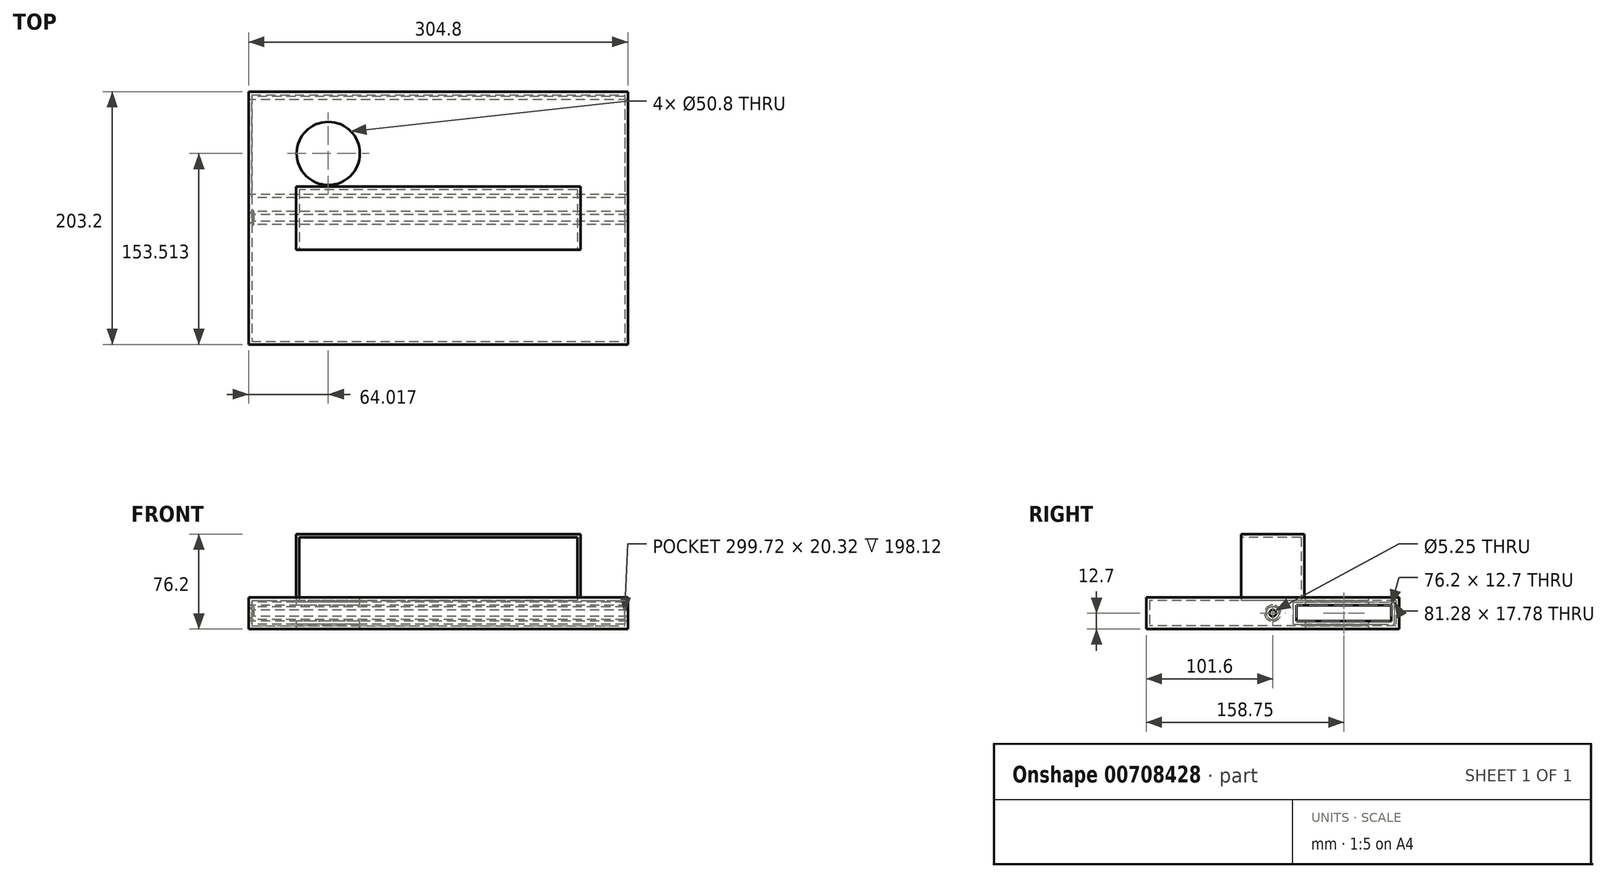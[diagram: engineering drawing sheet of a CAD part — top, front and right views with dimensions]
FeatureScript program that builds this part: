
annotation { "Feature Type Name" : "Feature", "Feature Type Description" : "" }
export const myFeature = defineFeature(function(context is Context, id is Id, definition is map)
    precondition{}
    {
        {
            var Q0;
            Q0=qCreatedBy(makeId("Top.planeOp"),FACE);
            var sketch = newSketch(context, id + "F0", { "sketchPlane" : qUnion([Q0])});
            skLineSegment(sketch, "E0.bottom", {"start": v(-152.4, 101.6) * mm, "end": v(152.4, 101.6) * mm});
            skLineSegment(sketch, "E0.top", {"start": v(-152.4, -101.6) * mm, "end": v(152.4, -101.6) * mm});
            skLineSegment(sketch, "E0.left", {"start": v(-152.4, 101.6) * mm, "end": v(-152.4, -101.6) * mm});
            skLineSegment(sketch, "E0.right", {"start": v(152.4, 101.6) * mm, "end": v(152.4, -101.6) * mm});
            skPoint(sketch, "E0.middle", {"position": v(0, 0) * mm});
            skSolve(sketch);
        }
        {
            var Q0;
            Q0=makeQuery(id+"F0.imprint","IMPRINT",FACE,{"disambiguationData":[TD([[makeQuery(id+"F0.imprint","IMPRINT",EDGE,{"derivedFrom":sQuery(id+"F0.wireOp",EDGE,"E0.bottom")}),-1.0]])]});
            extrude(context, id + "F1", {"entities" : qUnion([Q0]), "depth" : 25.4 * mm, "offsetDistance" : 25.4 * mm});
        }
        {
            var Q0;
            Q0=makeQuery(id+"F1.opExtrude","SWEPT_FACE",FACE,{"disambiguationData":[OSD([sQuery(id+"F0.wireOp",EDGE,"E0.left")])]});
            var sketch = newSketch(context, id + "F2", { "sketchPlane" : qUnion([Q0])});
            skLineSegment(sketch, "E1.bottom", {"start": v(-19.05, 6.35) * mm, "end": v(-95.25, 6.35) * mm});
            skLineSegment(sketch, "E1.top", {"start": v(-19.05, 19.05) * mm, "end": v(-95.25, 19.05) * mm});
            skLineSegment(sketch, "E1.left", {"start": v(-19.05, 6.35) * mm, "end": v(-19.05, 19.05) * mm});
            skLineSegment(sketch, "E1.right", {"start": v(-95.25, 6.35) * mm, "end": v(-95.25, 19.05) * mm});
            skPoint(sketch, "E1.middle", {"position": v(-57.15, 12.7) * mm});
            skPoint(sketch, "E1.middle.positionSnap0", {"position": v(-101.6, 12.7) * mm});
            skPoint(sketch, "E1.centerSnap0", {"position": v(-101.6, 12.7) * mm});
            skSolve(sketch);
        }
        {
            var Q0;
            Q0 = qSketchRegion(id + "F2", true);
            extrude(context, id + "F3", {"entities" : qUnion([Q0]), "operationType" : NewBodyOperationType.REMOVE, "oppositeDirection" : true, "depth" : 378.2 * mm, "offsetDistance" : 25.4 * mm});
        }
        {
            var Q0;
            Q0=makeQuery(id+"F1.opExtrude","CAP_FACE",FACE,{"disambiguationData":[OSD([sQuery(id+"F0.wireOp",EDGE,"E0.bottom"),sQuery(id+"F0.wireOp",EDGE,"E0.top"),sQuery(id+"F0.wireOp",EDGE,"E0.left"),sQuery(id+"F0.wireOp",EDGE,"E0.right")])],"isStart":false});
            var sketch = newSketch(context, id + "F4", { "sketchPlane" : qUnion([Q0])});
            skCircle(sketch, "E2", {"center": v(-88.38, 51.91) * mm, "radius": 25.4 * mm});
            skSolve(sketch);
        }
        {
            var Q0;
            Q0=makeQuery(id+"F1.opExtrude","SWEPT_FACE",FACE,{"disambiguationData":[OSD([sQuery(id+"F0.wireOp",EDGE,"E0.left")])]});
            var sketch = newSketch(context, id + "F5", { "sketchPlane" : qUnion([Q0])});
            skPoint(sketch, "E3", {"position": v(0, 12.7) * mm});
            skPoint(sketch, "E3.positionSnap0", {"position": v(-19.05, 12.7) * mm});
            skSolve(sketch);
        }
        {
            var Q0;
            Q0=sQuery(id+"F5.wireOp",VERTEX,"E3");
            var Q1;
            Q1=makeQuery(id+"F1.opExtrude","SWEPT_BODY",BODY,{"disambiguationData":[OSD([sQuery(id+"F0.wireOp",EDGE,"E0.bottom"),sQuery(id+"F0.wireOp",EDGE,"E0.top"),sQuery(id+"F0.wireOp",EDGE,"E0.left"),sQuery(id+"F0.wireOp",EDGE,"E0.right")])]});
            hole(context, id + "F6", {"style" : HoleStyle.C_SINK, "endStyle" : HoleEndStyle.THROUGH, "standardTappedOrClearance" : lookupTablePath({ "standard" : "ISO", "fit" : "Close", "size" : "M5", "type" : "Clearance" }), "standardBlindInLast" : lookupTablePath({ "fit" : "Close", "standard" : "ISO", "size" : "M5", "type" : "Clearance" }), "holeDiameter" : 5.25 * mm, "cSinkDiameter" : 11.2 * mm, "cSinkAngle" : 90 * degree, "majorDiameter" : 6.35 * mm, "isTappedThrough" : true, "tappedDepth" : 12.7 * mm, "tapClearance" : 3, "locations" : qUnion([Q0]), "scope" : qUnion([Q1])});
        }
        {
            var Q0;
            Q0=makeQuery(id+"F4.imprint","IMPRINT",FACE,{"disambiguationData":[TD([[makeQuery(id+"F4.imprint","IMPRINT",EDGE,{"derivedFrom":sQuery(id+"F4.wireOp",EDGE,"E2")}),-1.0]])]});
            var sketch = newSketch(context, id + "F7", { "sketchPlane" : qUnion([Q0])});
            skLineSegment(sketch, "E4.bottom", {"start": v(114.3, 25.4) * mm, "end": v(-114.3, 25.4) * mm});
            skLineSegment(sketch, "E4.top", {"start": v(114.3, -25.4) * mm, "end": v(-114.3, -25.4) * mm});
            skLineSegment(sketch, "E4.left", {"start": v(114.3, 25.4) * mm, "end": v(114.3, -25.4) * mm});
            skLineSegment(sketch, "E4.right", {"start": v(-114.3, 25.4) * mm, "end": v(-114.3, -25.4) * mm});
            skPoint(sketch, "E4.middle", {"position": v(0, 0) * mm});
            skSolve(sketch);
        }
        {
            var Q0;
            Q0=makeQuery(id+"F7.imprint","IMPRINT",FACE,{"disambiguationData":[TD([[makeQuery(id+"F7.imprint","IMPRINT",EDGE,{"derivedFrom":sQuery(id+"F7.wireOp",EDGE,"E4.bottom")}),1.0]])]});
            extrude(context, id + "F8", {"entities" : qUnion([Q0]), "operationType" : NewBodyOperationType.ADD, "depth" : 50.8 * mm, "offsetDistance" : 25.4 * mm});
        }
        {
            var Q0;
            Q0=makeQuery(id+"F8.opExtrude","SWEPT_FACE",FACE,{"disambiguationData":[OSD([sQuery(id+"F7.wireOp",EDGE,"E4.top")])]});
            var Q1;
            Q1=makeQuery(id+"F1.opExtrude","SWEPT_BODY",BODY,{"disambiguationData":[OSD([sQuery(id+"F0.wireOp",EDGE,"E0.bottom"),sQuery(id+"F0.wireOp",EDGE,"E0.top"),sQuery(id+"F0.wireOp",EDGE,"E0.left"),sQuery(id+"F0.wireOp",EDGE,"E0.right")])]});
            shell(context, id + "F9", {"entities" : qUnion([Q0]), "parts" : qUnion([Q1]), "thickness" : 2.54 * mm});
        }
        {
            var Q0;
            Q0=makeQuery(id+"F1.opExtrude","CAP_FACE",FACE,{"disambiguationData":[OSD([sQuery(id+"F0.wireOp",EDGE,"E0.bottom"),sQuery(id+"F0.wireOp",EDGE,"E0.top"),sQuery(id+"F0.wireOp",EDGE,"E0.left"),sQuery(id+"F0.wireOp",EDGE,"E0.right")])],"isStart":true});
            var sketch = newSketch(context, id + "F10", { "sketchPlane" : qUnion([Q0])});
            skLineSegment(sketch, "E5", {"start": v(0, 76.55) * mm, "end": v(0, -75.85) * mm});
            skSolve(sketch);
        }
        {
            var Q0;
            Q0=makeQuery(id+"F10.imprint","IMPRINT",FACE,{"disambiguationData":[TD([[makeQuery(id+"F10.imprint","IMPRINT",EDGE,{"derivedFrom":makeQuery(id+"F1.opExtrude","CAP_EDGE",EDGE,{"disambiguationData":[OSD([sQuery(id+"F0.wireOp",EDGE,"E0.bottom")])],"isStart":true})}),1.0]])]});
            var sketch = newSketch(context, id + "F11", { "sketchPlane" : qUnion([Q0])});
            skArc(sketch, "E6", {"start": v(0, 67.07) * mm, "mid": v(67.07, 0) * mm, "end": v(0, -67.07) * mm});
            skSolve(sketch);
        }
        {
            var Q0;
            Q0=makeQuery(id+"F10.imprint","IMPRINT",FACE,{"disambiguationData":[TD([[makeQuery(id+"F10.imprint","IMPRINT",EDGE,{"derivedFrom":makeQuery(id+"F1.opExtrude","CAP_EDGE",EDGE,{"disambiguationData":[OSD([sQuery(id+"F0.wireOp",EDGE,"E0.bottom")])],"isStart":true})}),1.0]])]});
            var Q1;
            Q1=sQuery(id+"F11.wireOp",EDGE,"E6");
            var Q2;
            Q2=sQuery(id+"F10.wireOp",EDGE,"E5");
            revolve(context, id + "F12", {"bodyType" : ToolBodyType.SURFACE, "operationType" : NewBodyOperationType.INTERSECT, "surfaceOperationType" : NewSurfaceOperationType.NEW, "entities" : qUnion([Q0]), "surfaceEntities" : qUnion([Q1]), "axis" : qUnion([Q2]), "revolveType" : RevolveType.ONE_DIRECTION, "angle" : 180 * degree});
        }
        {
            var Q0;
            Q0=makeQuery(id+"F4.imprint","IMPRINT",FACE,{"disambiguationData":[TD([[makeQuery(id+"F4.imprint","IMPRINT",EDGE,{"derivedFrom":sQuery(id+"F4.wireOp",EDGE,"E2")}),1.0]])]});
            extrude(context, id + "F13", {"entities" : qUnion([Q0]), "operationType" : NewBodyOperationType.REMOVE, "oppositeDirection" : true, "depth" : 25.4 * mm, "offsetDistance" : 25.4 * mm});
        }
    });
